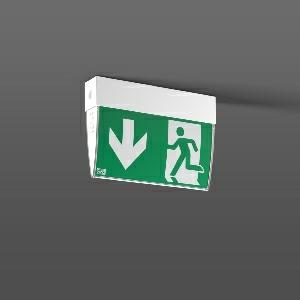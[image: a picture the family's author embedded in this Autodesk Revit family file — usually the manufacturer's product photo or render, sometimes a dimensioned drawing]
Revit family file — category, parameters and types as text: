
# Revit family: exeo_d_672400_002_e9a0
name_source: partatom
category: Lighting Fixtures
units: mm (PartAtom-declared; Revit-internal decimal feet)

## family parameters
Cut with Voids When Loaded = No
Host = Face
Light Source = No
Part Type = Normal
Room Calculation Point = No
Round Connector Dimension = Use Diameter
Shared = No

## types (1)
- EXEO D
    Apparent Load = 0 VA
    Default Elevation = 1800 mm
    Description = Series: EXEO D
self contained emergency luminaires for escape route identification Housing: shockproof plastic (polycarbonate). Includes 4 legends and 1 white lay in plastic sheet for fitting in the transparent cover. Mounting bracket for wall mounting and two sealing screws included in scope of delivery. Self-contained system with automatic self-test. 
Colour: white
Length: 255 mm
Width: 48 mm
Height: 177 mm
Weight: 750 g
Operating mode: non-maintained power mode
Viewing Distance: 24 m
Duration time: 3 h
Lamp: LED
Socket: without socket
Colour temperature: 4000K
Colour rendering index (CRI): 70
System power: 4 W
Control gear: electronic
Protection class: II
Type of protection: IP 54
    Height = 177 mm
    Lamp = 0 x
    Length = 255 mm
    Luminous efficacy = 0 lm/W
    Manufacturer = RZB
    ModVariant = No
    Model = 672400.002
    Mounting Place = Wall, Ceiling
    Mounting Type = Surface mounted
    Number of Poles = 1
    OnlyDefault = Yes
    Power Factor = 1
    Product Name = EXEO D
    Product group = Surface mounted ceiling and wall luminaires
    ProductGroupID = 305
    Protection Class = Protection class II
    Protection Degree = IP 54
    RLX_Detail_Level = 1
    RLX_Emergency_Light_Flux = 0 lm
    RLX_Emergency_Type = 0
    RLX_Emergency_Type_DB = No
    RlxData = <blob elided: 24149 chars, md5=e0484ab7>
    Standby Power = 0 W
    System Light Flux = 0 lm
    System Power = 0 W
    Type Comments = Product without accessories
    Type Image = 672400.002_decke.jpg
    URL = http://relux.com
    VarID = ---
    Voltage = 230 V
    Voltage Range = 220-240 V
    Weight = 0.00 kg
    Width = 48 mm  [stored 0.15748 ft]

note: [stored X ft] marks values corroborated as IEEE doubles in the binary element streams (Revit-internal decimal feet)

## geometry (parser evidence)
native form markers: Blend x4, Sweep x11
no freeform markers — native parametric forms only
